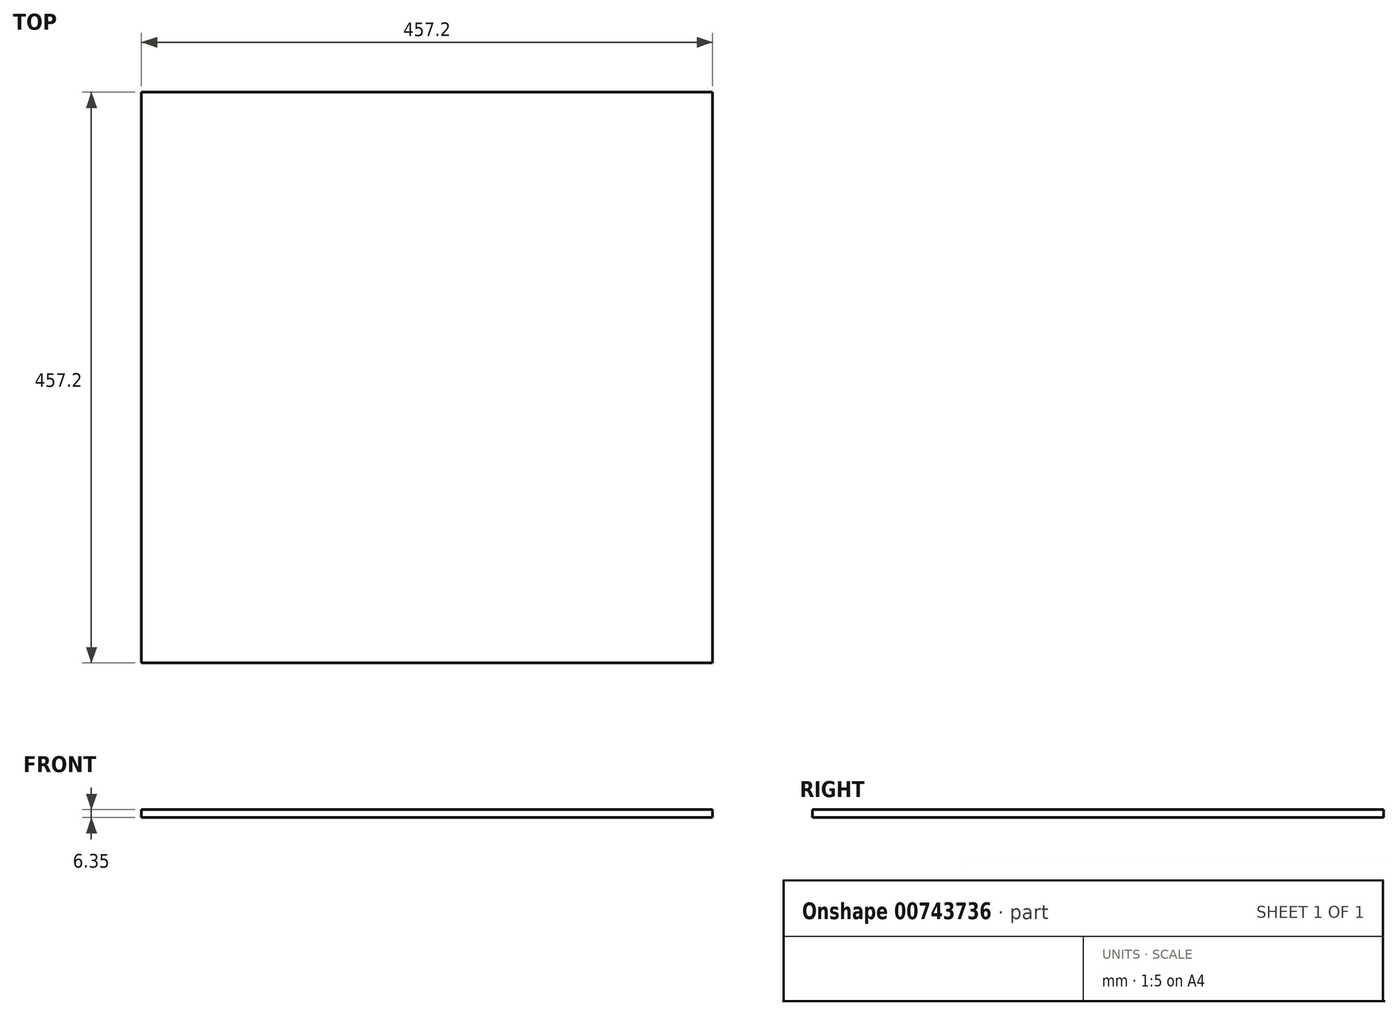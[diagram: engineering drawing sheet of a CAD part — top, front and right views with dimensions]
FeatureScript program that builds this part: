
annotation { "Feature Type Name" : "Feature", "Feature Type Description" : "" }
export const myFeature = defineFeature(function(context is Context, id is Id, definition is map)
    precondition{}
    {
        {
            var Q0;
            Q0=qCreatedBy(makeId("Top.planeOp"),FACE);
            var sketch = newSketch(context, id + "F0", { "sketchPlane" : qUnion([Q0])});
            skLineSegment(sketch, "E0.bottom", {"start": v(-228.6, 228.6) * mm, "end": v(228.6, 228.6) * mm});
            skLineSegment(sketch, "E0.top", {"start": v(-228.6, -228.6) * mm, "end": v(228.6, -228.6) * mm});
            skLineSegment(sketch, "E0.left", {"start": v(-228.6, 228.6) * mm, "end": v(-228.6, -228.6) * mm});
            skLineSegment(sketch, "E0.right", {"start": v(228.6, 228.6) * mm, "end": v(228.6, -228.6) * mm});
            skPoint(sketch, "E0.middle", {"position": v(0, 0) * mm});
            skSolve(sketch);
        }
        {
            var Q0;
            Q0 = qSketchRegion(id + "F0", true);
            extrude(context, id + "F1", {"entities" : qUnion([Q0]), "depth" : 6.35 * mm, "offsetDistance" : 25.4 * mm});
        }
    });
